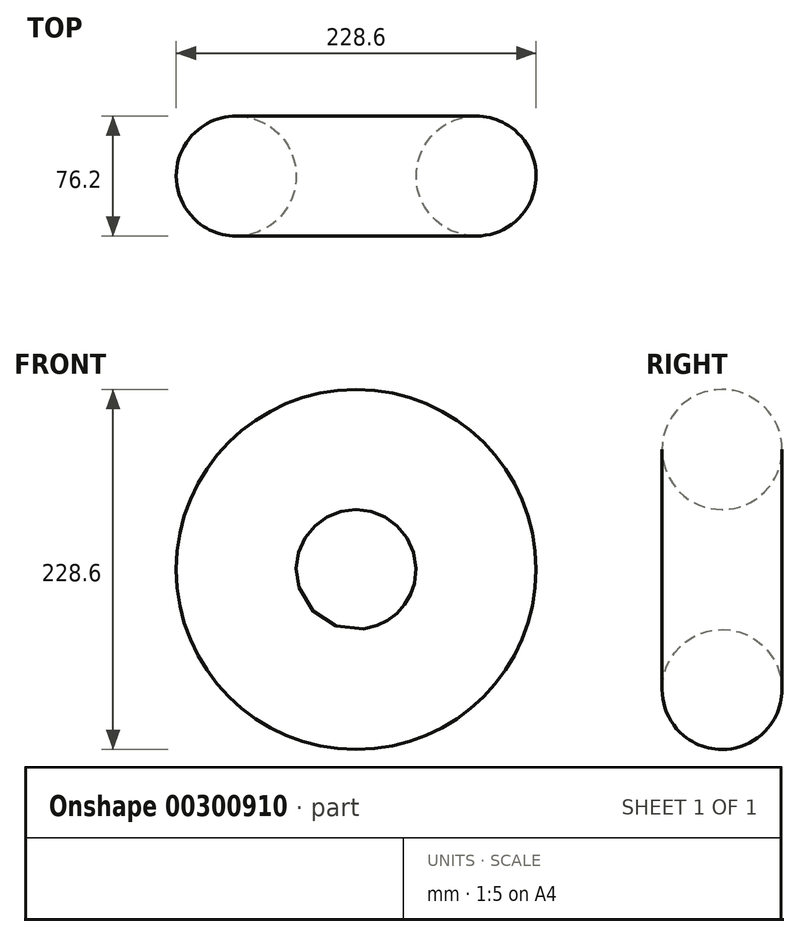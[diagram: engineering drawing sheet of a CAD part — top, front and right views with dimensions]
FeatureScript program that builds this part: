
annotation { "Feature Type Name" : "Feature", "Feature Type Description" : "" }
export const myFeature = defineFeature(function(context is Context, id is Id, definition is map)
    precondition{}
    {
        {
            var Q0;
            Q0=qCreatedBy(makeId("Top.planeOp"),FACE);
            var sketch = newSketch(context, id + "F0", { "sketchPlane" : qUnion([Q0])});
            skCircle(sketch, "E0", {"center": v(0, 0) * mm, "radius": 38.1 * mm});
            skSolve(sketch);
        }
        {
            var Q0;
            Q0=qCreatedBy(makeId("Front.planeOp"),FACE);
            var sketch = newSketch(context, id + "F1", { "sketchPlane" : qUnion([Q0])});
            skCircle(sketch, "E1", {"center": v(-76.2, 0) * mm, "radius": 38.1 * mm});
            skSolve(sketch);
        }
        {
            var Q0;
            Q0=makeQuery(id+"F0.imprint","IMPRINT",FACE,{"disambiguationData":[TD([[makeQuery(id+"F0.imprint","IMPRINT",EDGE,{"derivedFrom":sQuery(id+"F0.wireOp",EDGE,"E0")}),1.0]])]});
            var Q1;
            Q1=sQuery(id+"F1.wireOp",EDGE,"E1");
            revolve(context, id + "F2", {"entities" : qUnion([Q0]), "axis" : qUnion([Q1]), "revolveType" : RevolveType.FULL});
        }
    });
